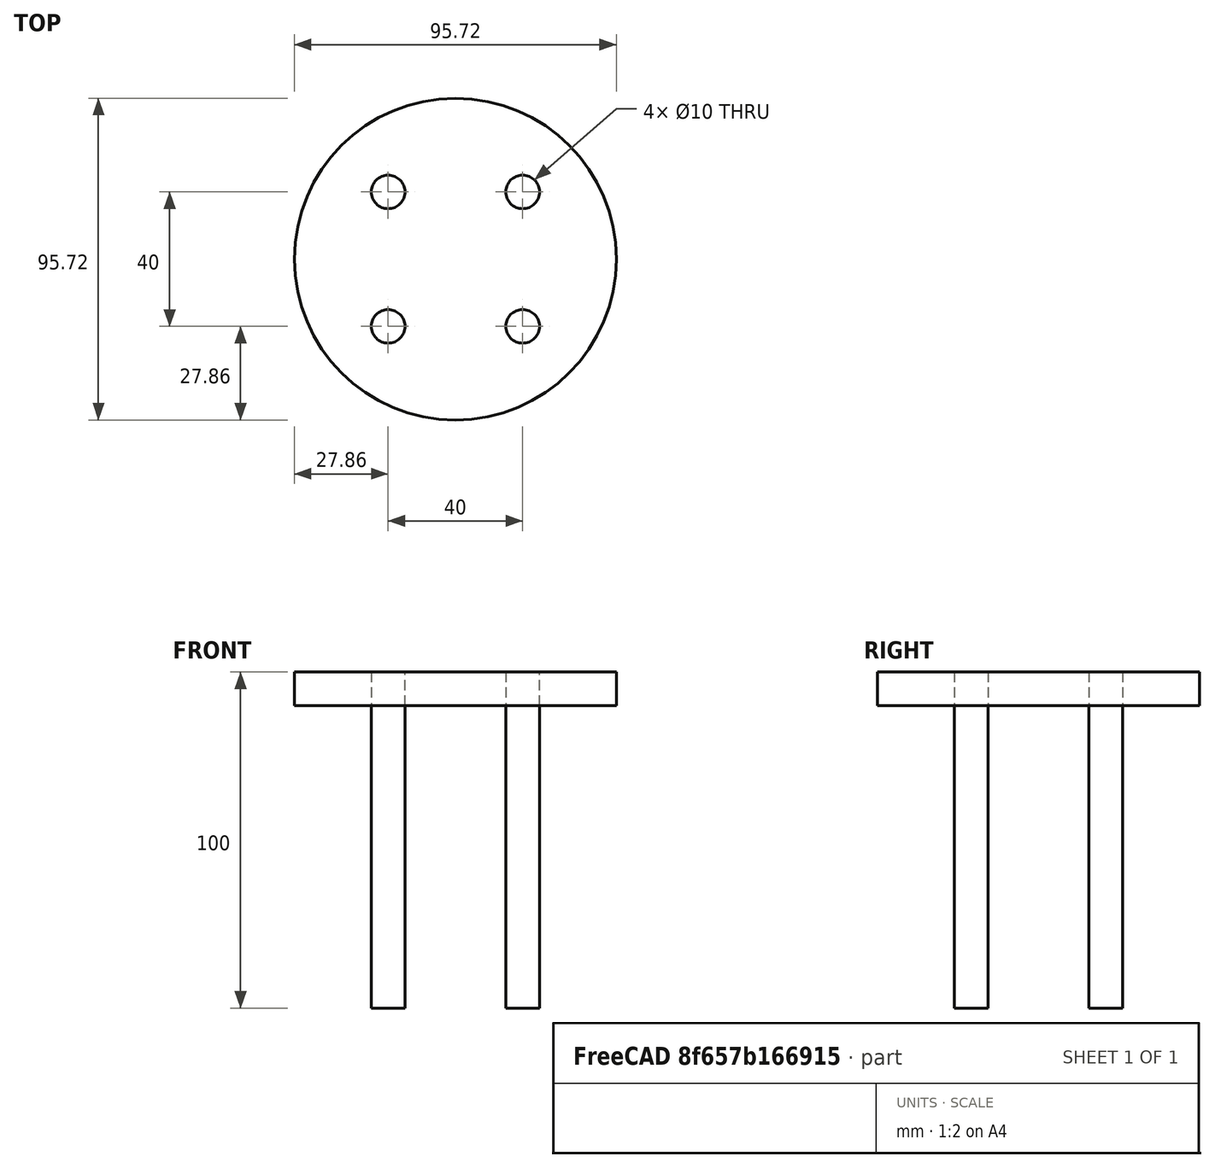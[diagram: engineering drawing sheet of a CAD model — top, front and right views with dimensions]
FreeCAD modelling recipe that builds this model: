
FCSTD DOCUMENT  (FreeCAD 0.21R33694 (Git))
Label: OJT1_T19R03_tamboret
License: All rights reserved
LicenseURL: http://en.wikipedia.org/wiki/All_rights_reserved
objects: Part::Cylinder×4, Sketcher::SketchObject×1, PartDesign::Pad×1, PartDesign::Body×1
note: 8 computed .brp shape members not serialized (recipe doc carries the construction recipe); baked Part::Feature solids carry a one-line shape summary decoded from their .brp

FEATURE [Sketcher::SketchObject] Sketch
  FullyConstrained = false
  MapMode = 5
  Support = -> [XY_Plane]
  sketch-geometry (5):
    g0: Circle CenterX=0 CenterY=0 CenterZ=0 NormalX=0 NormalY=0 NormalZ=1 AngleXU=0 Radius=47.8617
    g1: Circle CenterX=-20 CenterY=20 CenterZ=0 NormalX=0 NormalY=0 NormalZ=1 AngleXU=0 Radius=5
    g2: Circle CenterX=-20 CenterY=-20 CenterZ=0 NormalX=0 NormalY=0 NormalZ=1 AngleXU=0 Radius=5
    g3: Circle CenterX=20 CenterY=20 CenterZ=0 NormalX=0 NormalY=0 NormalZ=1 AngleXU=0 Radius=5
    g4: Circle CenterX=20 CenterY=-20 CenterZ=0 NormalX=0 NormalY=0 NormalZ=1 AngleXU=0 Radius=5
  constraints (9):
    c: Diameter(g1) = 10
    c: Diameter(g3) = 10
    c: Diameter(g2) = 10
    c: Diameter(g4) = 10
    c: Symmetric(g1,g3,g-2)
    c: Symmetric(g2,g4,g-2)
    c: Symmetric(g1,g2,g-1)
    c: DistanceX(g1,g3) = 40
    c: DistanceY(g2,g1) = 40
FEATURE [PartDesign::Pad] Pad
  Direction = (0,0,1)
  Length = 10
  Length2 = 10
  Profile = -> Sketch
  ReferenceAxis = -> Sketch [N_Axis]
  Type = 0
FEATURE [PartDesign::Body] Body
  Group = -> [Sketch,Pad]
  Origin = -> Origin
  Tip = -> Pad
FEATURE [Part::Cylinder] Cylinder
  Angle = 360
  AttacherType = Attacher::AttachEngine3D
  FirstAngle = 0
  Height = 100
  Placement = pos=(20,-20,-90) rot=(0,0,1;0rad)
  Radius = 5
  SecondAngle = 0
FEATURE [Part::Cylinder] Cylinder001
  Angle = 360
  AttacherType = Attacher::AttachEngine3D
  FirstAngle = 0
  Height = 100
  Placement = pos=(20,20,-90) rot=(0,0,1;0rad)
  Radius = 5
  SecondAngle = 0
FEATURE [Part::Cylinder] Cylinder002
  Angle = 360
  AttacherType = Attacher::AttachEngine3D
  FirstAngle = 0
  Height = 100
  Placement = pos=(-20,20,-90) rot=(0,0,1;0rad)
  Radius = 5
  SecondAngle = 0
FEATURE [Part::Cylinder] Cylinder003
  Angle = 360
  AttacherType = Attacher::AttachEngine3D
  FirstAngle = 0
  Height = 100
  Placement = pos=(-20,-20,-90) rot=(0,0,1;0rad)
  Radius = 5
  SecondAngle = 0
